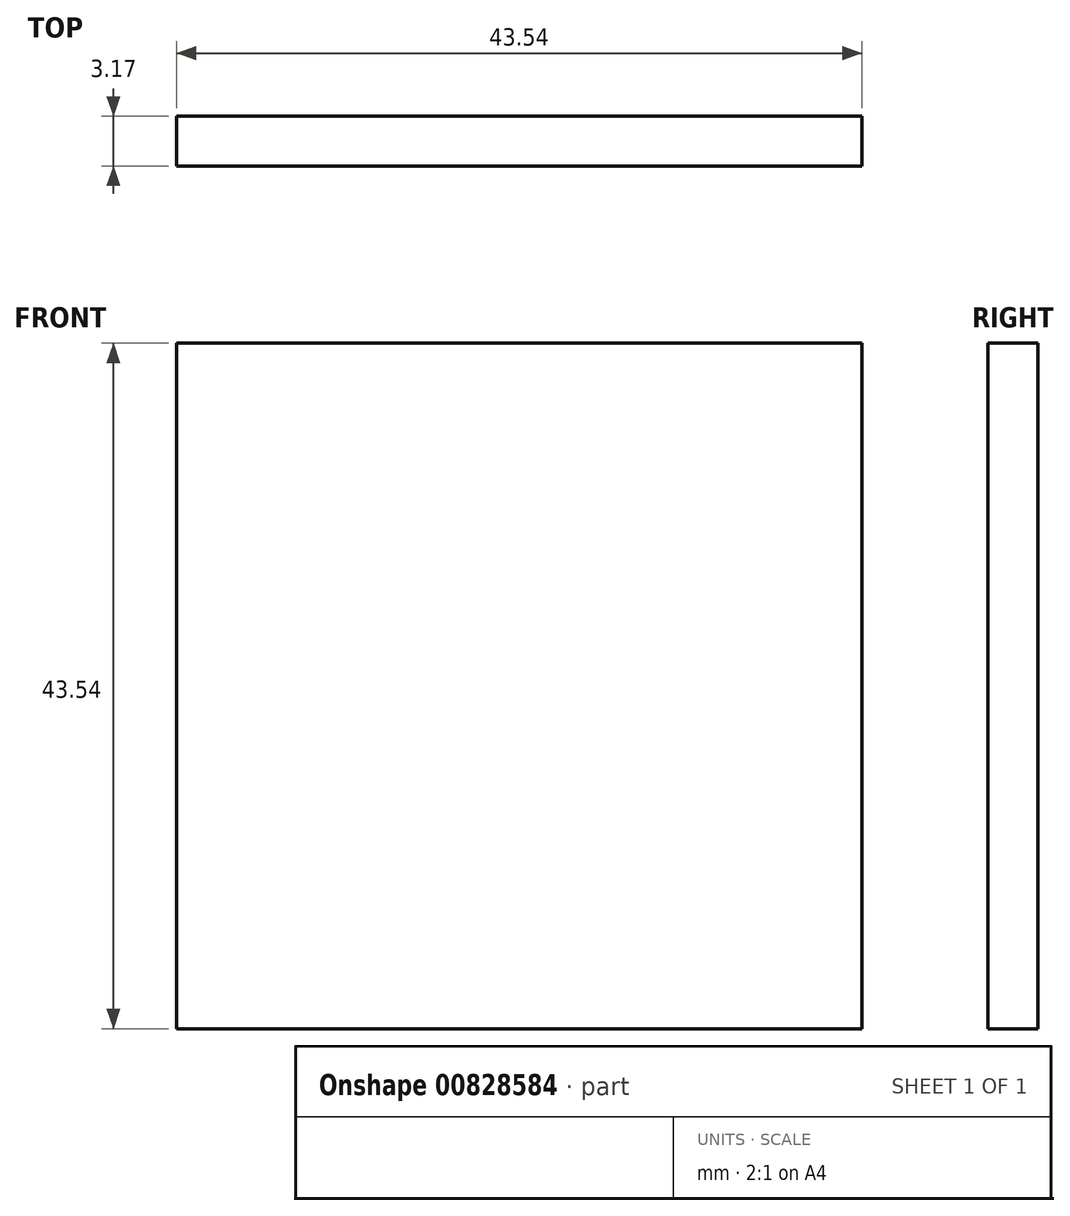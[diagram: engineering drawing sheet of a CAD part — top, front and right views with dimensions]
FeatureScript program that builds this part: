
annotation { "Feature Type Name" : "Feature", "Feature Type Description" : "" }
export const myFeature = defineFeature(function(context is Context, id is Id, definition is map)
    precondition{}
    {
        {
            var Q0;
            Q0=qCreatedBy(makeId("Front.planeOp"),FACE);
            var sketch = newSketch(context, id + "F0", { "sketchPlane" : qUnion([Q0])});
            skLineSegment(sketch, "E0.bottom", {"start": v(0, 0) * mm, "end": v(43.54, 0) * mm});
            skLineSegment(sketch, "E0.top", {"start": v(0, 43.54) * mm, "end": v(43.54, 43.54) * mm});
            skLineSegment(sketch, "E0.left", {"start": v(0, 0) * mm, "end": v(0, 43.54) * mm});
            skLineSegment(sketch, "E0.right", {"start": v(43.54, 0) * mm, "end": v(43.54, 43.54) * mm});
            skSolve(sketch);
        }
        {
            var Q0;
            Q0=makeQuery(id+"F0.imprint","IMPRINT",FACE,{"disambiguationData":[TD([[makeQuery(id+"F0.imprint","IMPRINT",EDGE,{"derivedFrom":sQuery(id+"F0.wireOp",EDGE,"E0.bottom")}),1.0]])]});
            extrude(context, id + "F1", {"entities" : qUnion([Q0]), "depth" : 3.17 * mm, "offsetDistance" : 25.4 * mm});
        }
    });
